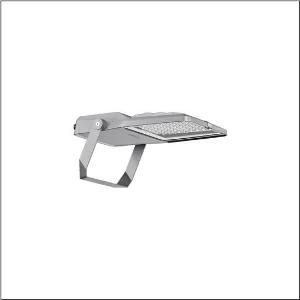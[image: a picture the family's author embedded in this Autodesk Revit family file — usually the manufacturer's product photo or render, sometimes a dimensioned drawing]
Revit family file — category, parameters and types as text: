
# Revit family: floodlight_fl_21_mini___pl43_5xa7775d2a1a_a4ba
name_source: partatom
category: Lighting Fixtures
units: mm (PartAtom-declared; Revit-internal decimal feet)

## family parameters
Cut with Voids When Loaded = No
Host = Face
Light Source = No
Part Type = Normal
Room Calculation Point = No
Round Connector Dimension = Use Diameter
Shared = No

## types (1)
- --- (1 x LED, 18300 lm, 142.9 W, 3000K)
    Apparent Load = 143 VA
    CIE Flux Codes = 27 78 99 100 100
    Color Rendering = 70
    Color Temperature = 3000K
    Default Elevation = 1800 mm
    Description = Floodlight FL 21 mini, floodlight, primary light control with lens, of PMMA, primary optical cover: protective disc, of toughened safety glass, transparent, light distribution: PL43, light emission: direct distribution, installation type: surface-mounted, LED, High Power LED, rated luminous flux: 18.300lm, luminous efficacy: 128lm/W, light colour: 730, colour temperature: 3000K, control gear: Smart Interface (Zhaga), control: flexible luminous flux parameterisation, time-dependent luminous flux control, constant luminous flux control, overheat protection, pre-setting: logarithmic dimming characteristic, with terminal, 6-pole, mains connection: 220..240V, AC, 50/60Hz, start of lifetime: 143W, end of service life: 151W, reduction: 63W, luminaire housing, of diecast aluminium, powder-coated, SITECO metallic grey (DB 702S), corrosivity category C5 mid according to DIN EN ISO 12944, suitable for swimming pools, chlorine-resistant, sealing non-destructively replaceable, mounting bracket, of steel, galvanised, powder-coated, SITECO metallic grey (DB 702S), Smart Interface above, protection rating (complete): IP66, insulation class (complete): insulation class II (safety insulation), certification: CE, ENEC, VDE, protection symbol: D, impact resistance: IK08, permissible operating ambient temperature: -40..+40°C, permissible operating ambient temperature for outdoor applications: -40..+50°C, standard: DIN EN 12944, LABS conformity tested according to VDMA 24364:2018-05, packaging unit: 1 piece

Light Distribution: PL43
    Height = 70 mm
    Lamp = 1 x LED
    Lamp Light Flux = 18300 lm
    Lamp Power = 142.9 W
    Lamp count = 1
    Length = 485 mm
    Luminous efficacy = 128 lm/W
    Manufacturer = Siteco
    ModVariant = No
    Model = 5XA7775D2A1A
    Mounting Place = Pole
    Mounting Type = Pole annexe
    Number of Poles = 1
    OnlyDefault = Yes
    Power Factor = 1
    Product Name = Floodlight FL 21 mini | PL43
    Product group = floodlight | pylon annexe
    ProductGroupID = 6201
    Protection Class = Protection class II
    Protection Degree = IP 66
    RLX_Detail_Level = 1
    RLX_Emergency_Light_Flux = 0 lm
    RLX_Emergency_Type = 0
    RLX_Emergency_Type_DB = No
    RlxData = <blob elided: 96245 chars, md5=59b70383>
    Socket = socket
    Standby Power = 0 W
    System Light Flux = 18300 lm
    System Power = 143 W
    Type Comments = factory setting: luminous flux: 100 % | dim-lin: 254 | 730 mA
    Type Image = l_1006845.jpg
    URL = http://relux.com
    VarID = @adj_162069
    Voltage = 0 V
    Weight = 0.00 kg
    Width = 337 mm

## geometry (parser evidence)
native form markers: Blend x4, Sweep x10
no freeform markers — native parametric forms only
